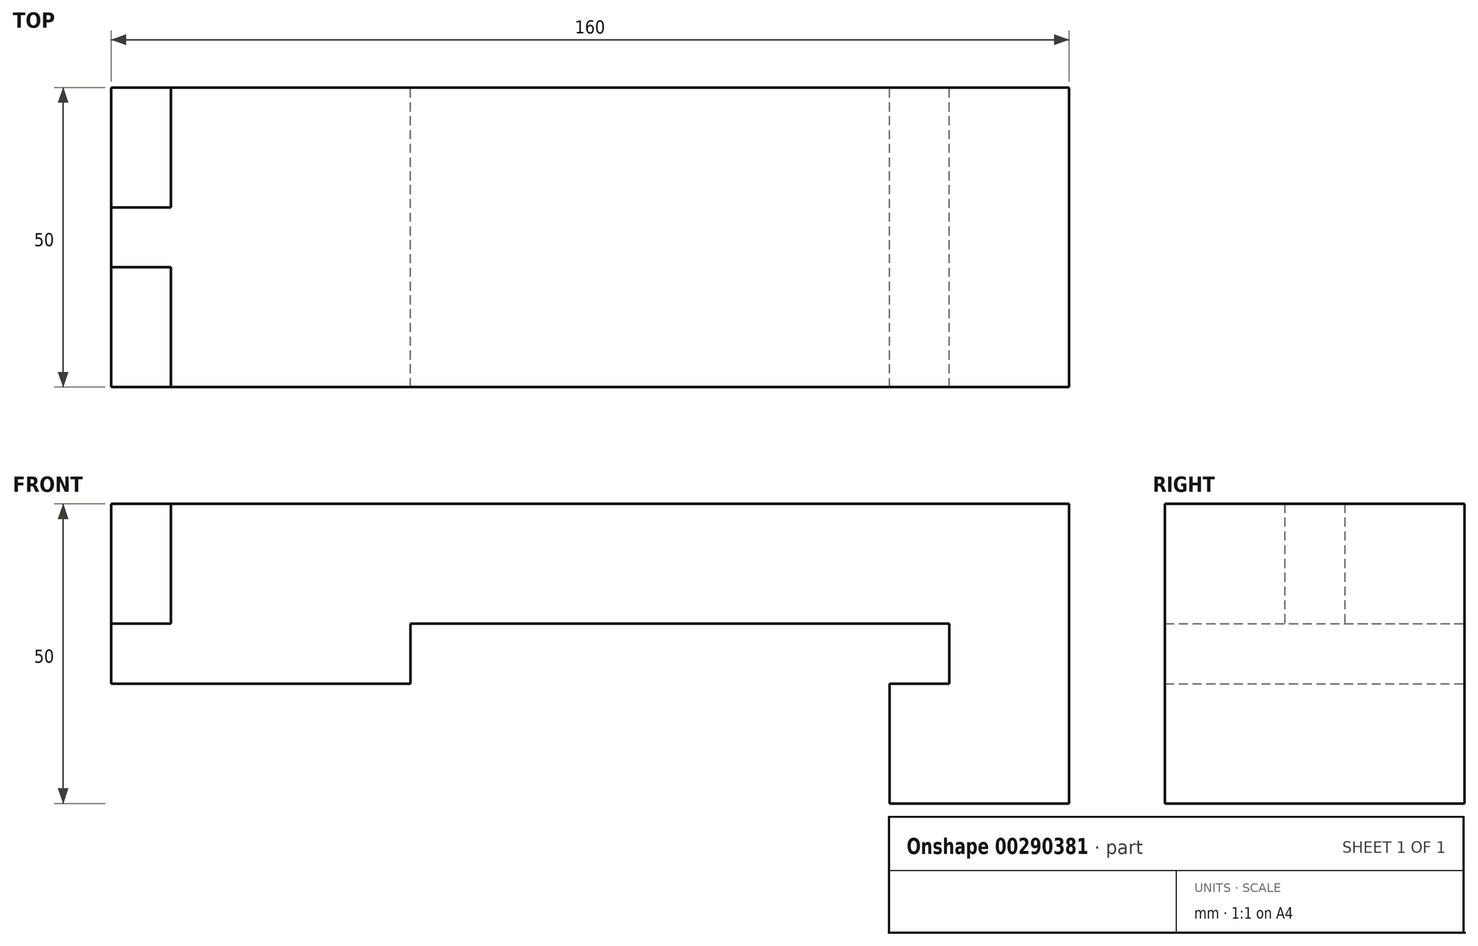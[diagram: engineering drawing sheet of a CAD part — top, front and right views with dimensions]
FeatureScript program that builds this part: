
annotation { "Feature Type Name" : "Feature", "Feature Type Description" : "" }
export const myFeature = defineFeature(function(context is Context, id is Id, definition is map)
    precondition{}
    {
        {
            var Q0;
            Q0=qCreatedBy(makeId("Front.planeOp"),FACE);
            var sketch = newSketch(context, id + "F0", { "sketchPlane" : qUnion([Q0])});
            skLineSegment(sketch, "E0", {"start": v(0, 0) * mm, "end": v(0, 20) * mm});
            skLineSegment(sketch, "E1", {"start": v(0, 20) * mm, "end": v(10, 20) * mm});
            skLineSegment(sketch, "E2", {"start": v(10, 20) * mm, "end": v(10, 30) * mm});
            skLineSegment(sketch, "E3", {"start": v(10, 30) * mm, "end": v(-80, 30) * mm});
            skLineSegment(sketch, "E4", {"start": v(-80, 30) * mm, "end": v(-80, 20) * mm});
            skLineSegment(sketch, "E5", {"start": v(-80, 20) * mm, "end": v(-130, 20) * mm});
            skLineSegment(sketch, "E6", {"start": v(-130, 20) * mm, "end": v(-130, 30) * mm});
            skLineSegment(sketch, "E7", {"start": v(-130, 30) * mm, "end": v(-120, 30) * mm});
            skLineSegment(sketch, "E8", {"start": v(-120, 30) * mm, "end": v(-120, 50) * mm});
            skLineSegment(sketch, "E9", {"start": v(-120, 50) * mm, "end": v(30, 50) * mm});
            skLineSegment(sketch, "E10", {"start": v(30, 50) * mm, "end": v(30, 0) * mm});
            skLineSegment(sketch, "E11", {"start": v(30, 0) * mm, "end": v(0, 0) * mm});
            skSolve(sketch);
        }
        {
            var Q0;
            Q0 = qSketchRegion(id + "F0", true);
            extrude(context, id + "F1", {"entities" : qUnion([Q0]), "endBound" : BoundingType.SYMMETRIC, "depth" : 50 * mm});
        }
        {
            var Q0;
            Q0=makeQuery(id+"F1.opExtrude","SWEPT_FACE",FACE,{"disambiguationData":[OSD([sQuery(id+"F0.wireOp",EDGE,"E7")])]});
            var sketch = newSketch(context, id + "F2", { "sketchPlane" : qUnion([Q0])});
            skLineSegment(sketch, "E12", {"start": v(-130, 0) * mm, "end": v(-120, 0) * mm, "construction": true});
            skLineSegment(sketch, "E13.bottom", {"start": v(-130, 5) * mm, "end": v(-120, 5) * mm});
            skLineSegment(sketch, "E13.top", {"start": v(-130, -5) * mm, "end": v(-120, -5) * mm});
            skLineSegment(sketch, "E13.left", {"start": v(-130, 5) * mm, "end": v(-130, -5) * mm});
            skLineSegment(sketch, "E13.right", {"start": v(-120, 5) * mm, "end": v(-120, -5) * mm});
            skSolve(sketch);
        }
        {
            var Q0;
            Q0 = qSketchRegion(id + "F2", true);
            var Q1;
            Q1=makeQuery(id+"F1.opExtrude","SWEPT_FACE",FACE,{"disambiguationData":[OSD([sQuery(id+"F0.wireOp",EDGE,"E9")])]});
            extrude(context, id + "F3", {"entities" : qUnion([Q0]), "operationType" : NewBodyOperationType.ADD, "endBound" : BoundingType.UP_TO_SURFACE, "endBoundEntityFace" : qUnion([Q1]), "depth" : 25 * mm});
        }
    });
